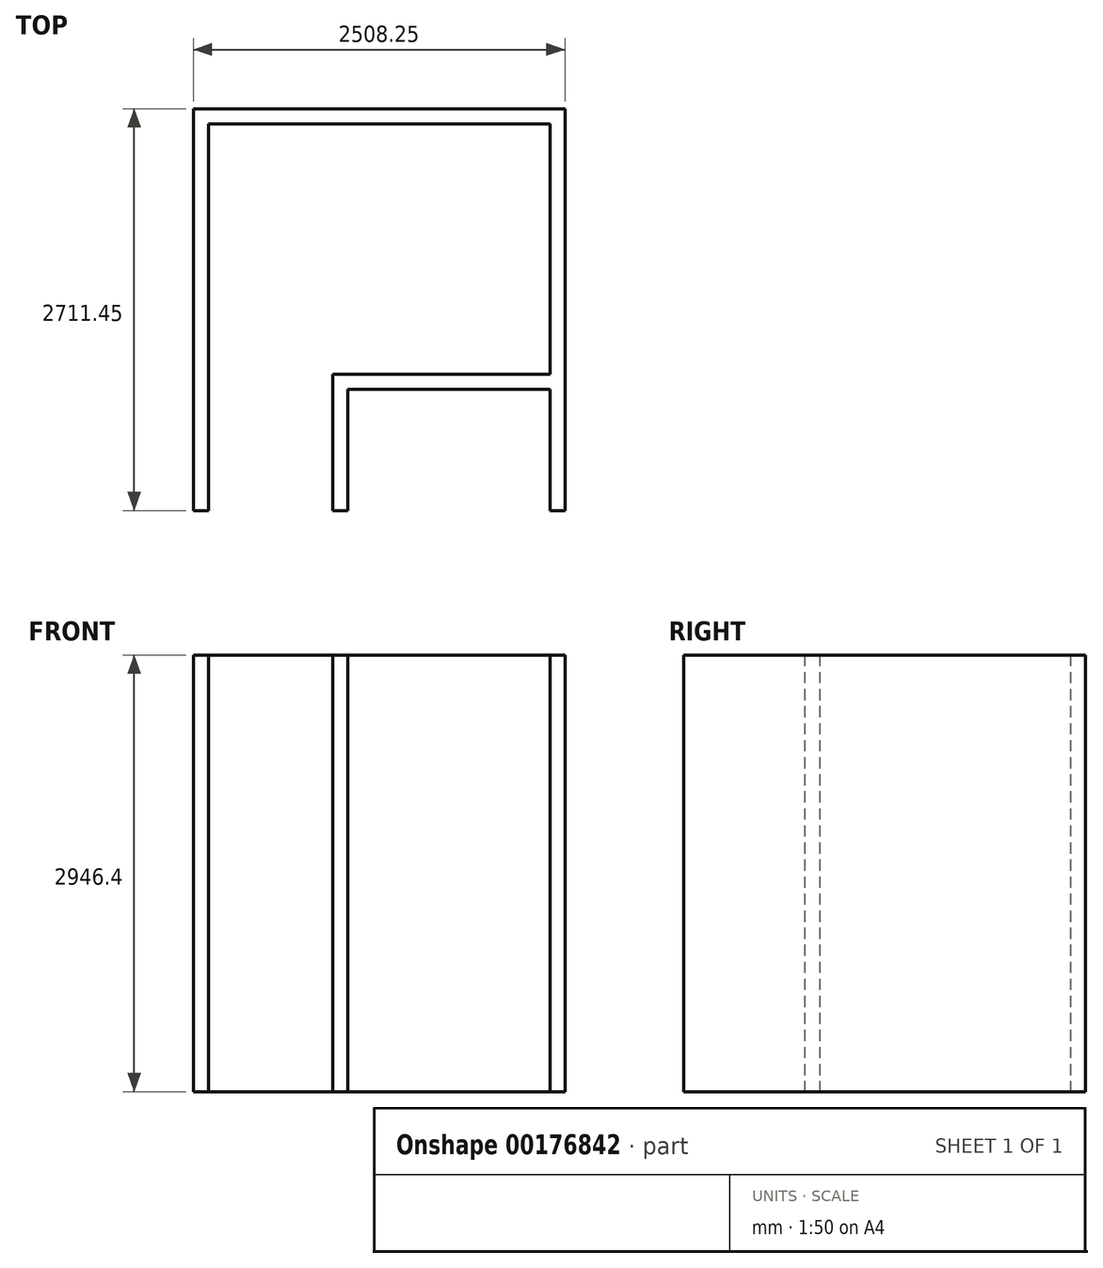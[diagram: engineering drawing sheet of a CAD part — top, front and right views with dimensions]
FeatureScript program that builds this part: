
annotation { "Feature Type Name" : "Feature", "Feature Type Description" : "" }
export const myFeature = defineFeature(function(context is Context, id is Id, definition is map)
    precondition{}
    {
        {
            var Q0;
            Q0=qCreatedBy(makeId("Top.planeOp"),FACE);
            var sketch = newSketch(context, id + "F0", { "sketchPlane" : qUnion([Q0])});
            skLineSegment(sketch, "E0.top", {"start": v(-611.94, 2609.85) * mm, "end": v(-2916.99, 2609.85) * mm});
            skLineSegment(sketch, "E0.left", {"start": v(-611.94, 0) * mm, "end": v(-611.94, 2609.85) * mm});
            skLineSegment(sketch, "E0.right", {"start": v(-2916.99, 0) * mm, "end": v(-2916.99, 2609.85) * mm});
            skLineSegment(sketch, "E1.0", {"start": v(-510.34, 2711.45) * mm, "end": v(-3018.59, 2711.45) * mm});
            skLineSegment(sketch, "E1.1", {"start": v(-510.34, 0) * mm, "end": v(-510.34, 2711.45) * mm});
            skLineSegment(sketch, "E1.3", {"start": v(-3018.59, 0) * mm, "end": v(-3018.59, 2711.45) * mm});
            skLineSegment(sketch, "E2", {"start": v(-2916.99, 0) * mm, "end": v(-3018.59, 0) * mm});
            skLineSegment(sketch, "E3", {"start": v(-611.94, 0) * mm, "end": v(-510.34, 0) * mm});
            skLineSegment(sketch, "E4.top", {"start": v(-2078.79, 0) * mm, "end": v(-1977.19, 0) * mm});
            skLineSegment(sketch, "E4.left", {"start": v(-2078.79, 917.9) * mm, "end": v(-2078.79, 0) * mm});
            skLineSegment(sketch, "E4.right", {"start": v(-1977.19, 816.3) * mm, "end": v(-1977.19, 0) * mm});
            skLineSegment(sketch, "E5.bottom", {"start": v(-2078.79, 917.9) * mm, "end": v(-611.94, 917.9) * mm});
            skLineSegment(sketch, "E5.top", {"start": v(-1977.19, 816.3) * mm, "end": v(-611.94, 816.3) * mm});
            skLineSegment(sketch, "E5.right", {"start": v(-611.94, 917.9) * mm, "end": v(-611.94, 816.3) * mm});
            skSolve(sketch);
        }
        {
            var Q0;
            {var subQ1=sQuery(id+"F0.wireOp",EDGE,"E0.top");Q0=makeQuery(id+"F0.imprint","IMPRINT",FACE,{"disambiguationData":[TD([[makeQuery(id+"F0.imprint","IMPRINT",EDGE,{"derivedFrom":subQ1}),-1.0]])]});}
            var Q1;
            Q1=makeQuery(id+"F0.imprint","IMPRINT",FACE,{"disambiguationData":[TD([[makeQuery(id+"F0.imprint","IMPRINT",EDGE,{"derivedFrom":sQuery(id+"F0.wireOp",EDGE,"E4.top")}),1.0]])]});
            extrude(context, id + "F1", {"entities" : qUnion([Q0, Q1]), "depth" : 2946.4 * mm});
        }
    });
